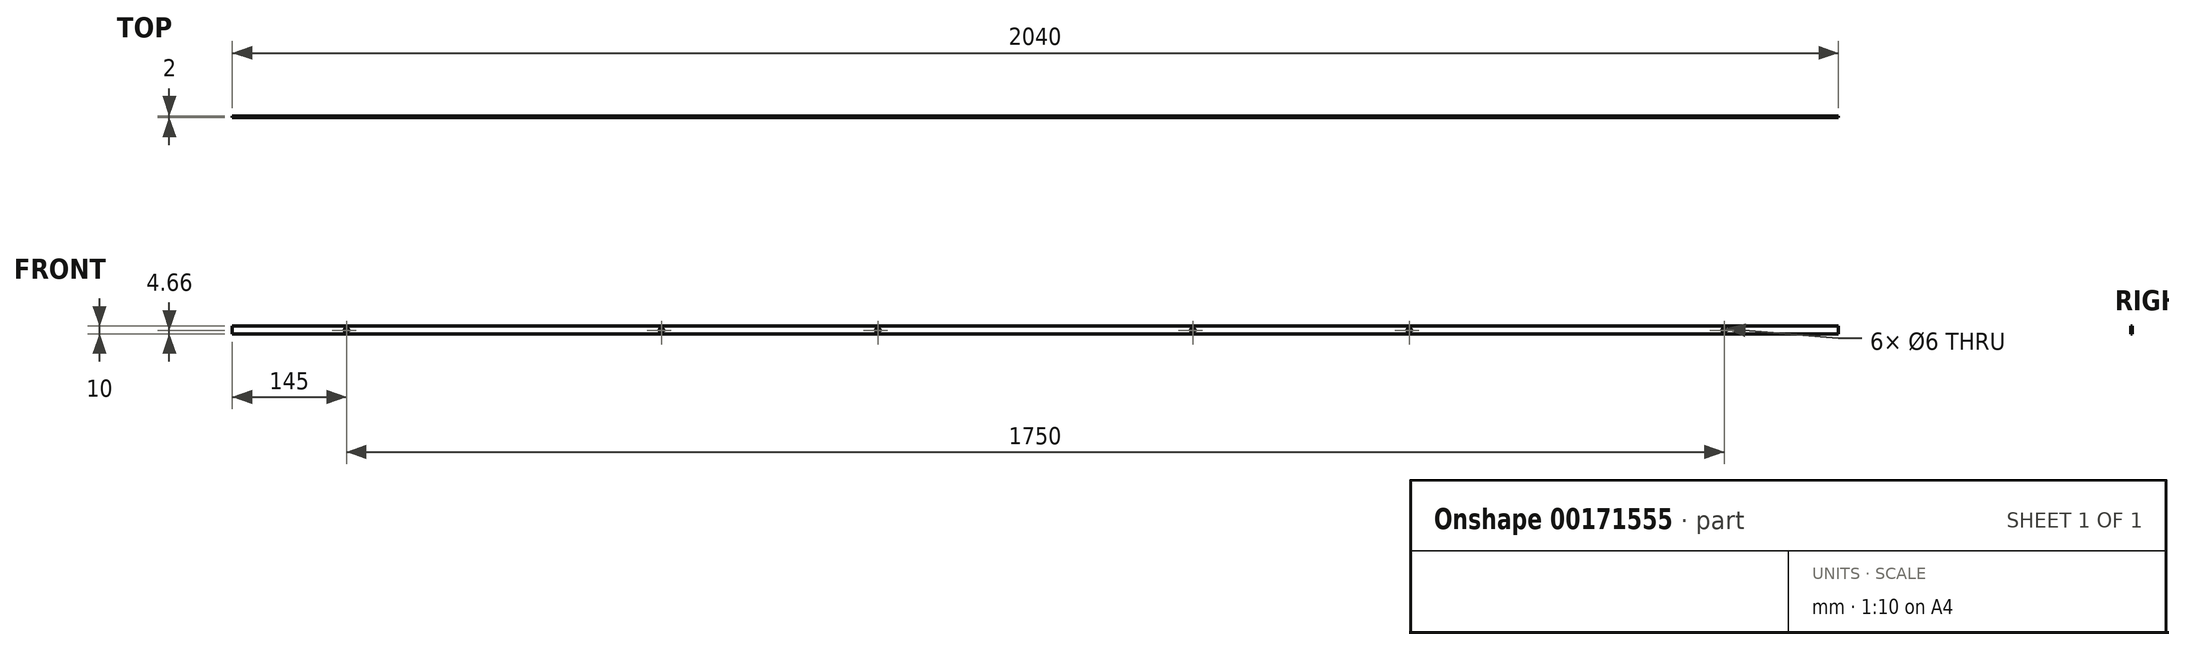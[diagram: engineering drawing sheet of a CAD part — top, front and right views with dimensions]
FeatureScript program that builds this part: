
annotation { "Feature Type Name" : "Feature", "Feature Type Description" : "" }
export const myFeature = defineFeature(function(context is Context, id is Id, definition is map)
    precondition{}
    {
        {
            var Q0;
            Q0=qCreatedBy(makeId("Front.planeOp"),FACE);
            var sketch = newSketch(context, id + "F0", { "sketchPlane" : qUnion([Q0])});
            skLineSegment(sketch, "E0.bottom", {"start": v(0, 0) * mm, "end": v(2040, 0) * mm});
            skLineSegment(sketch, "E0.top", {"start": v(0, 10) * mm, "end": v(2040, 10) * mm});
            skLineSegment(sketch, "E0.left", {"start": v(0, 0) * mm, "end": v(0, 10) * mm});
            skLineSegment(sketch, "E0.right", {"start": v(2040, 0) * mm, "end": v(2040, 10) * mm});
            skSolve(sketch);
        }
        {
            var Q0;
            Q0 = qSketchRegion(id + "F0", true);
            extrude(context, id + "F1", {"entities" : qUnion([Q0]), "depth" : 2 * mm});
        }
        {
            var Q0;
            Q0=makeQuery(id+"F1.opExtrude","CAP_FACE",FACE,{"disambiguationData":[OSD([sQuery(id+"F0.wireOp",EDGE,"E0.bottom"),sQuery(id+"F0.wireOp",EDGE,"E0.top"),sQuery(id+"F0.wireOp",EDGE,"E0.left"),sQuery(id+"F0.wireOp",EDGE,"E0.right")])],"isStart":false});
            var sketch = newSketch(context, id + "F2", { "sketchPlane" : qUnion([Q0])});
            skCircle(sketch, "E1", {"center": v(145, 4.66) * mm, "radius": 3 * mm});
            skCircle(sketch, "E2", {"center": v(545, 4.66) * mm, "radius": 3 * mm});
            skCircle(sketch, "E3.1.0.0", {"center": v(820, 4.66) * mm, "radius": 3 * mm});
            skCircle(sketch, "E3.1.0.1", {"center": v(1220, 4.66) * mm, "radius": 3 * mm});
            skCircle(sketch, "E3.2.0.0", {"center": v(1495, 4.66) * mm, "radius": 3 * mm});
            skCircle(sketch, "E3.2.0.1", {"center": v(1895, 4.66) * mm, "radius": 3 * mm});
            skLineSegment(sketch, "E3.direction1", {"start": v(145, 4.66) * mm, "end": v(820, 4.66) * mm, "construction": true});
            skSolve(sketch);
        }
        {
            var Q0;
            Q0 = qSketchRegion(id + "F2", true);
            extrude(context, id + "F3", {"entities" : qUnion([Q0]), "operationType" : NewBodyOperationType.REMOVE, "endBound" : BoundingType.THROUGH_ALL, "oppositeDirection" : true, "depth" : 25 * mm});
        }
    });
